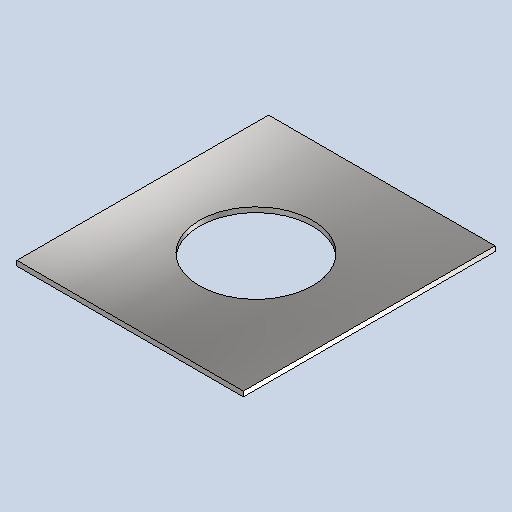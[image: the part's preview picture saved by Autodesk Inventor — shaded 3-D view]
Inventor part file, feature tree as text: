
AUTODESK INVENTOR PART (.ipt)
format: ipt  version: 2025 (Build 290162010, 162A)  size: 136,192 bytes
history: native  units: mm
features: sketch x2, other x2, sheet_metal_op x1, extrude x1
ambient origin geometry x8: Origin, YZ Plane, XZ Plane, XY Plane, X Axis, Y Axis, Z Axis, Center Point
bodies: Solid1 (feature_tree)
feature tree (6):
  sheet_metal_op  "Face1"
  extrude  "Extrusion1"  Depth=200.0mm
  sketch  "Sketch1"  dims[d0=180.0mm d1=200.0mm]
  other  "Plate1"
  sketch  "Sketch2"  dims[d2=4.0mm d3=90.0mm d4=10.0mm d5=0.0mm]
  other  "Definition1"
